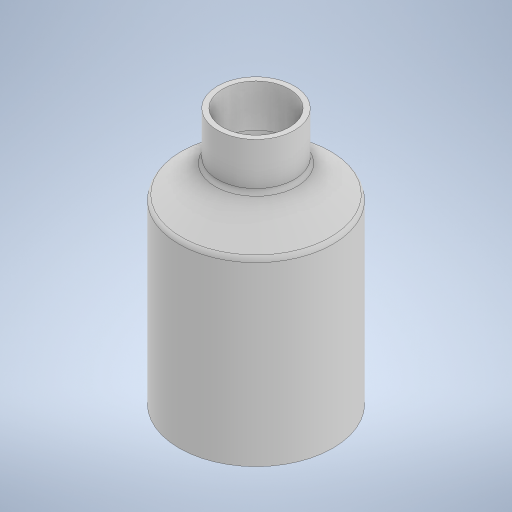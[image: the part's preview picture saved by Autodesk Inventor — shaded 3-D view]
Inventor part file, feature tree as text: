
AUTODESK INVENTOR PART (.ipt)
format: ipt  version: 2024.2 (Build 282272000, 272)  size: 257,536 bytes
history: native  units: in
note: dims shown in document units (in); Inventor stores cm internally (conversion verified against a paired STEP export)
features: revolve x1, shell x1, sketch x1
ambient origin geometry x8: Origin, YZ Plane, XZ Plane, XY Plane, X Axis, Y Axis, Z Axis, Center Point
bodies: Solid1 (feature_tree)
feature tree (3):
  revolve  "Revolution1"  [1 undecoded]
  shell  "Shell1"  Thickness=0.75in
  sketch  "Sketch1"  dims[d0=5.0in d1=1.5in d2=0.75in d3=0.125in d4=90.0deg d5=0.1in]
note: 1 required parameter value undecoded (feature->parameter linkage not recoverable at this tier; creation-order binding heuristic only, values carry confidence <= 0.55)
